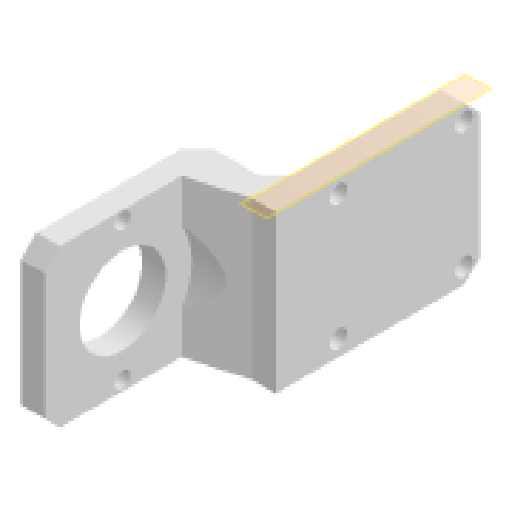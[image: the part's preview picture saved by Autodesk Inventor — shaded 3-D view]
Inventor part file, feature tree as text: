
AUTODESK INVENTOR PART (.ipt)
format: ipt  version: 2024.1 (Build 281209000, 209)  size: 173,056 bytes
history: native  units: mm
features: extrude x5, sketch x5, projected_geometry x4, plane x1, chamfer x1
ambient origin geometry x8: Origin, YZ Plane, XZ Plane, XY Plane, X Axis, Y Axis, Z Axis, Center Point
bodies: Volumenkörper1 (feature_tree)
feature tree (16):
  extrude  "Extrusion1"  Depth=40.0mm
  plane  "Arbeitsebene1"
  extrude  "Extrusion2"  Depth=32.0mm
  chamfer  "Fasen1"  Distance=4.5mm
  extrude  "Extrusion3"  Depth=10.0mm
  extrude  "Extrusion4"  Depth=6.0mm TaperAngle=0.0deg
  extrude  "Extrusion5"  TaperAngle=0.0deg  [1 undecoded]
  sketch  "Skizze1"  dims[d0=40.0mm d1=40.0mm]
  sketch  "Skizze2"  dims[d2=32.0mm d3=32.0mm]
  projected_geometry  "Projizierte Kontur1"
  sketch  "Skizze3"  dims[d4=4.5mm]
  projected_geometry  "Projizierte Kontur2"
  sketch  "Skizze4"  dims[d5=4.5mm]
  projected_geometry  "Projizierte Kontur3"
  sketch  "Skizze5"  dims[d6=4.5mm d7=4.5mm d8=12.0mm d9=6.0mm d10=0.0mm d11=0.0mm d12=6.0mm d13=45.0mm d14=6.0mm d15=14.0mm d16=10.0mm d17=6.0mm d18=0.0mm d19=4.0mm d20=2.0mm d21=45.0deg d22=35.0mm d23=0.0mm d24=0.0mm d25=4.0mm d26=4.0mm d27=10.0mm d28=0.0mm d29=22.0mm d30=10.0mm d31=0.0mm]
  projected_geometry  "Projizierte Kontur4"
note: 1 required parameter value undecoded (feature->parameter linkage not recoverable at this tier; creation-order binding heuristic only, values carry confidence <= 0.55)
